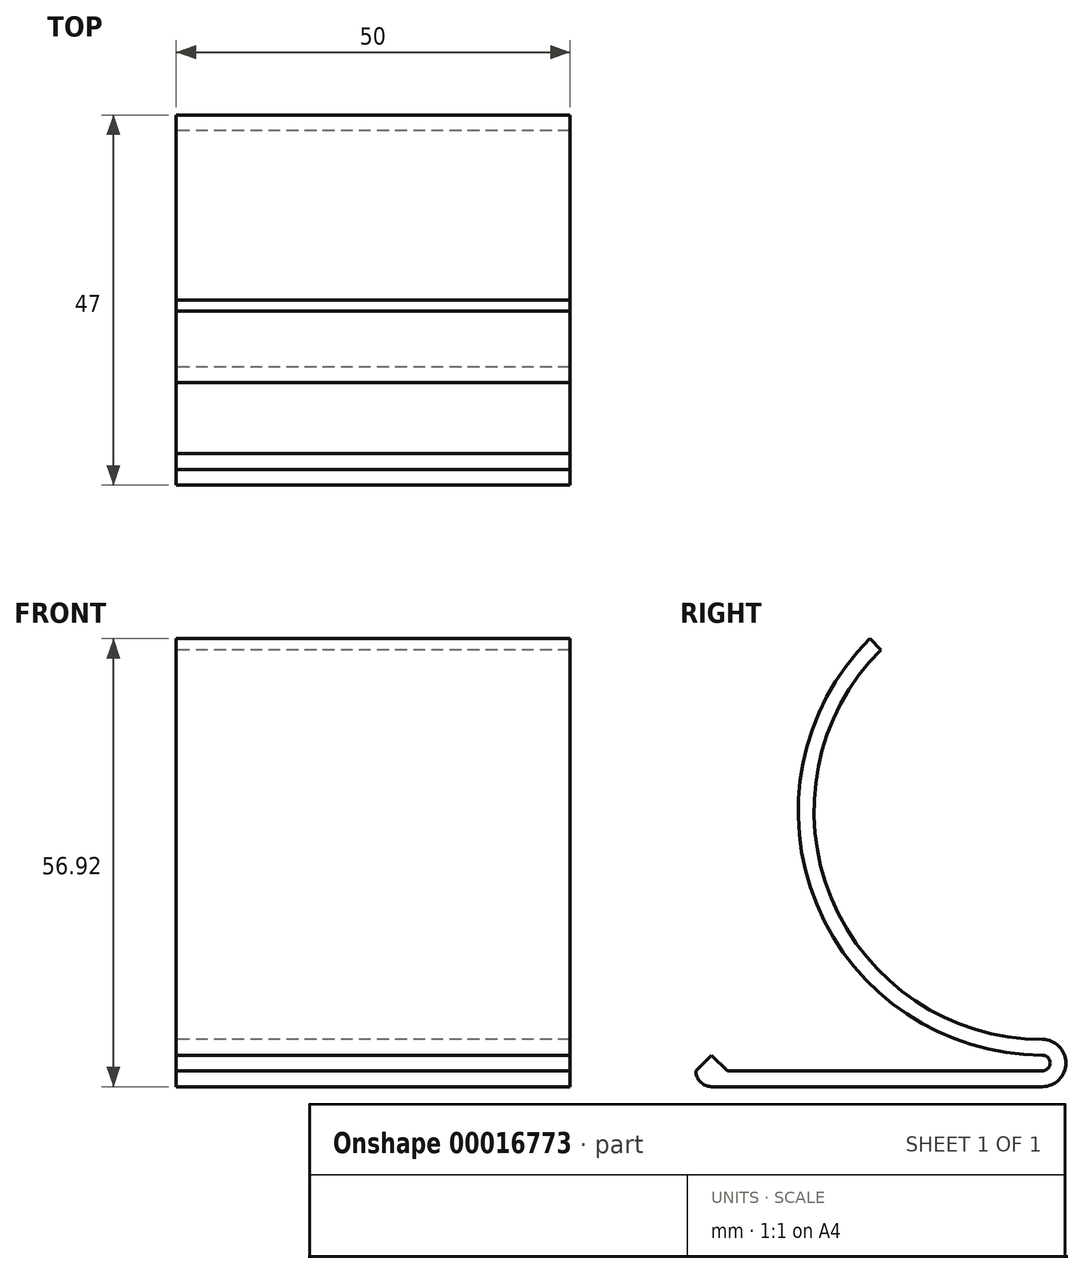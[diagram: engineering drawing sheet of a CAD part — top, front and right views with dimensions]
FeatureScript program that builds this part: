
annotation { "Feature Type Name" : "Feature", "Feature Type Description" : "" }
export const myFeature = defineFeature(function(context is Context, id is Id, definition is map)
    precondition{}
    {
        {
            var Q0;
            Q0=qCreatedBy(makeId("Right.planeOp"),FACE);
            var sketch = newSketch(context, id + "F0", { "sketchPlane" : qUnion([Q0])});
            skArc(sketch, "E0", {"start": v(-20.5, 20.5) * mm, "mid": v(-26.8, -11.1) * mm, "end": v(0, -29) * mm});
            skArc(sketch, "E1", {"start": v(-21.92, 21.92) * mm, "mid": v(-28.64, -11.86) * mm, "end": v(0, -31) * mm});
            skLineSegment(sketch, "E2", {"start": v(0, -35) * mm, "end": v(-42, -35) * mm});
            skLineSegment(sketch, "E3", {"start": v(0, -33) * mm, "end": v(-40, -33) * mm});
            skArc(sketch, "E4", {"start": v(0, -33) * mm, "mid": v(1, -32) * mm, "end": v(0, -31) * mm});
            skArc(sketch, "E5", {"start": v(0, -35) * mm, "mid": v(3, -32) * mm, "end": v(0, -29) * mm});
            skLineSegment(sketch, "E6", {"start": v(-20.5, 20.5) * mm, "end": v(-21.92, 21.92) * mm});
            skLineSegment(sketch, "E7", {"start": v(-42, -31) * mm, "end": v(-40, -33) * mm, "construction": true});
            skLineSegment(sketch, "E8", {"start": v(-44, -33) * mm, "end": v(-42, -31) * mm});
            skLineSegment(sketch, "E9", {"start": v(-42, -31) * mm, "end": v(-40, -33) * mm});
            skArc(sketch, "E10", {"start": v(-44, -33) * mm, "mid": v(-43.41, -34.41) * mm, "end": v(-42, -35) * mm});
            skLineSegment(sketch, "E11", {"start": v(-38.78, -33) * mm, "end": v(-17.48, 66.34) * mm, "construction": true});
            skLineSegment(sketch, "E12", {"start": v(-17.48, 66.34) * mm, "end": v(-19.03, 66.67) * mm, "construction": true});
            skLineSegment(sketch, "E13", {"start": v(-19.03, 66.67) * mm, "end": v(-40.33, -32.67) * mm, "construction": true});
            skLineSegment(sketch, "E14", {"start": v(-40.33, -32.67) * mm, "end": v(-38.78, -33) * mm, "construction": true});
            skSolve(sketch);
        }
        {
            var Q0;
            Q0=makeQuery(id+"F0.imprint","IMPRINT",FACE,{"disambiguationData":[TD([[makeQuery(id+"F0.imprint","IMPRINT",EDGE,{"derivedFrom":sQuery(id+"F0.wireOp",EDGE,"E0")}),-1.0]])]});
            extrude(context, id + "F1", {"entities" : qUnion([Q0]), "depth" : 50 * mm});
        }
    });
